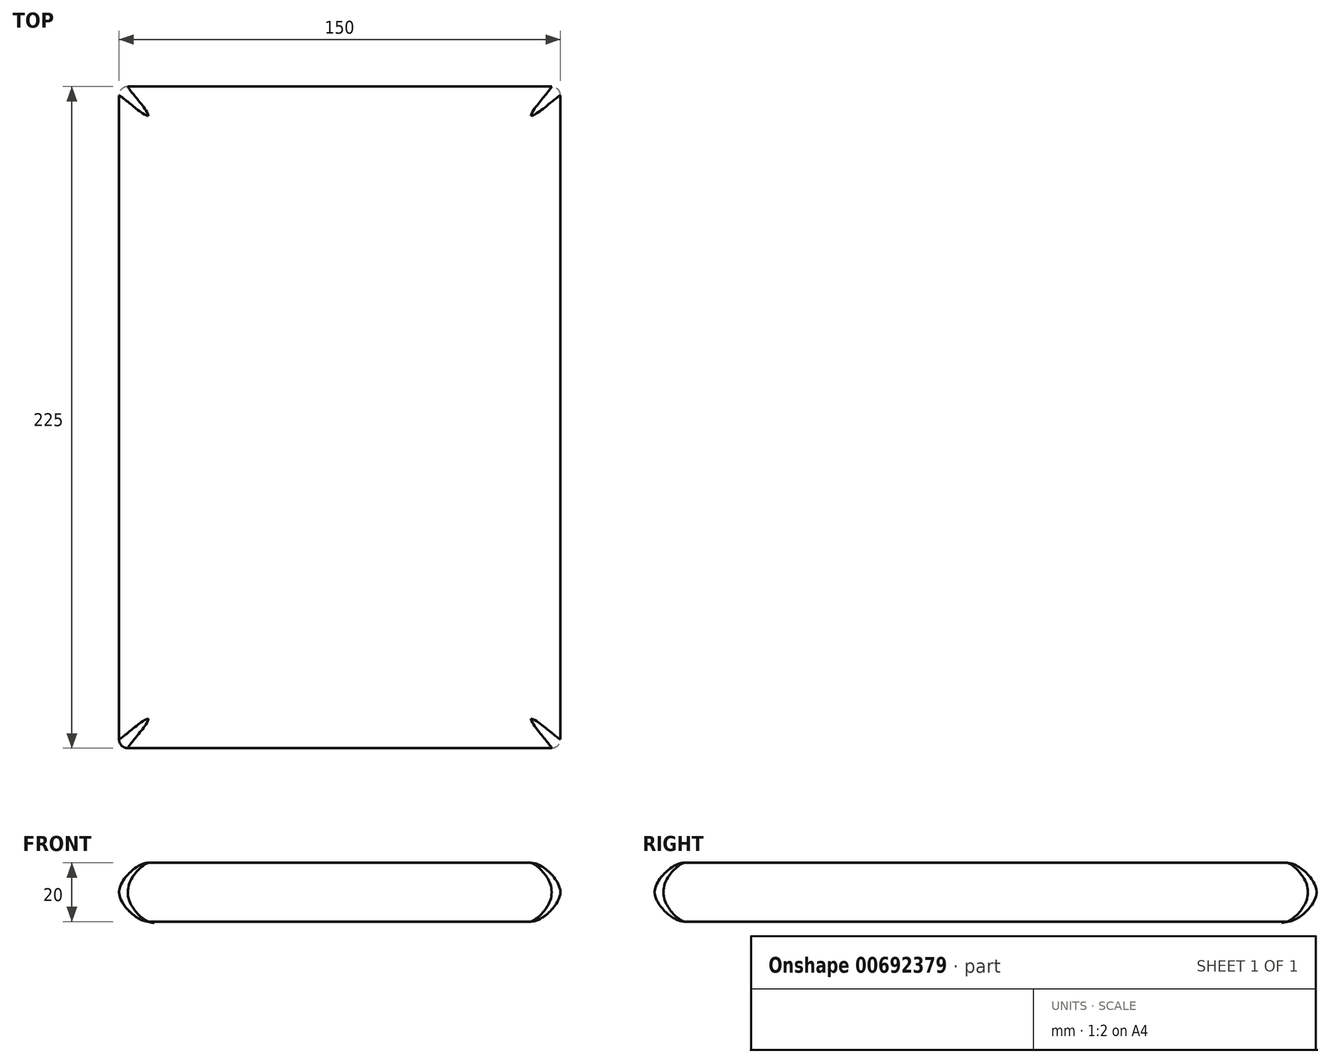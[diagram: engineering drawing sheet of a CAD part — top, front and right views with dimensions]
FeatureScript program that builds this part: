
annotation { "Feature Type Name" : "Feature", "Feature Type Description" : "" }
export const myFeature = defineFeature(function(context is Context, id is Id, definition is map)
    precondition{}
    {
        {
            var Q0;
            Q0=qCreatedBy(makeId("Right.planeOp"),FACE);
            var sketch = newSketch(context, id + "F0", { "sketchPlane" : qUnion([Q0])});
            skLineSegment(sketch, "E0.bottom", {"start": v(-112.5, 17.5) * mm, "end": v(-87.5, 17.5) * mm});
            skLineSegment(sketch, "E0.top", {"start": v(-112.5, 2.5) * mm, "end": v(-87.5, 2.5) * mm});
            skLineSegment(sketch, "E0.left", {"start": v(-112.5, 17.5) * mm, "end": v(-112.5, 2.5) * mm});
            skLineSegment(sketch, "E0.right", {"start": v(-87.5, 17.5) * mm, "end": v(-87.5, 2.5) * mm});
            skLineSegment(sketch, "E1.bottom", {"start": v(-132.5, 20) * mm, "end": v(0, 20) * mm});
            skLineSegment(sketch, "E1.top", {"start": v(-132.5, 0) * mm, "end": v(0, 0) * mm});
            skLineSegment(sketch, "E1.left", {"start": v(-132.5, 20) * mm, "end": v(-132.5, 0) * mm, "construction": true});
            skLineSegment(sketch, "E1.right", {"start": v(0, 20) * mm, "end": v(0, 0) * mm});
            skPoint(sketch, "E2", {"position": v(-112.5, 10) * mm});
            skPoint(sketch, "E3", {"position": v(-112.5, 20) * mm});
            skLineSegment(sketch, "E4", {"start": v(-112.5, 10) * mm, "end": v(-132.5, 10) * mm, "construction": true});
            skEllipticalArc(sketch, "E5", {});
            skLineSegment(sketch, "E6", {"start": v(-87.5, 17.5) * mm, "end": v(0, 17.5) * mm});
            skLineSegment(sketch, "E7", {"start": v(-87.5, 2.5) * mm, "end": v(0, 2.5) * mm});
            skLineSegment(sketch, "E8", {"start": v(0, 0) * mm, "end": v(0, -20.03) * mm, "construction": true});
            const initialGuessF0  = {"E5": [-0.1125, 0.01, -1, 0, 0.02, 0.01, 4.71238898038469, 1.5707963267948966]};
            skSetInitialGuess(sketch, initialGuessF0);
            skSolve(sketch);
        }
        {
            var Q0;
            Q0=qCreatedBy(makeId("Top.planeOp"),FACE);
            var sketch = newSketch(context, id + "F1", { "sketchPlane" : qUnion([Q0])});
            skLineSegment(sketch, "E9.bottom", {"start": v(-75, 112.5) * mm, "end": v(75, 112.5) * mm});
            skLineSegment(sketch, "E9.top", {"start": v(-75, -112.5) * mm, "end": v(75, -112.5) * mm});
            skLineSegment(sketch, "E9.left", {"start": v(-75, 112.5) * mm, "end": v(-75, -112.5) * mm});
            skLineSegment(sketch, "E9.right", {"start": v(75, 112.5) * mm, "end": v(75, -112.5) * mm});
            skPoint(sketch, "E10", {"position": v(0, 112.5) * mm});
            skPoint(sketch, "E11", {"position": v(-75, 0) * mm});
            skLineSegment(sketch, "E12", {"start": v(-75, 0) * mm, "end": v(0, 0) * mm, "construction": true});
            skLineSegment(sketch, "E13", {"start": v(0, 0) * mm, "end": v(0, 112.5) * mm, "construction": true});
            skSolve(sketch);
        }
        {
            var Q0;
            Q0=makeQuery(id+"F1.imprint","IMPRINT",FACE,{"disambiguationData":[TD([[makeQuery(id+"F1.imprint","IMPRINT",EDGE,{"derivedFrom":sQuery(id+"F1.wireOp",EDGE,"E9.bottom")}),-1.0]])]});
            extrude(context, id + "F2", {"entities" : qUnion([Q0]), "depth" : 20 * mm, "offsetDistance" : 25 * mm});
        }
        {
            var Q0;
            Q0=makeQuery(id+"F2.opExtrude","CAP_FACE",FACE,{"disambiguationData":[OSD([sQuery(id+"F1.wireOp",EDGE,"E9.bottom"),sQuery(id+"F1.wireOp",EDGE,"E9.top"),sQuery(id+"F1.wireOp",EDGE,"E9.left"),sQuery(id+"F1.wireOp",EDGE,"E9.right")])],"isStart":false});
            var Q1;
            Q1=makeQuery(id+"F2.opExtrude","CAP_FACE",FACE,{"disambiguationData":[OSD([sQuery(id+"F1.wireOp",EDGE,"E9.bottom"),sQuery(id+"F1.wireOp",EDGE,"E9.top"),sQuery(id+"F1.wireOp",EDGE,"E9.left"),sQuery(id+"F1.wireOp",EDGE,"E9.right")])],"isStart":true});
            fillet(context, id + "F3", {"entities" : qUnion([Q0, Q1]), "radius" : 10 * mm, "tangentPropagation" : true, "rho" : 0.3, "crossSection" : FilletCrossSection.CONIC, "allowEdgeOverflow" : false});
        }
        {
            var Q0;
            Q0=makeQuery(id+"F3.opFillet","BLEND_EDGE",EDGE,{"blendedFrom":[makeQuery(id+"F2.opExtrude","CAP_EDGE",EDGE,{"disambiguationData":[OSD([sQuery(id+"F1.wireOp",EDGE,"E9.top")])],"isStart":false}),makeQuery(id+"F2.opExtrude","CAP_EDGE",EDGE,{"disambiguationData":[OSD([sQuery(id+"F1.wireOp",EDGE,"E9.right")])],"isStart":false})],"blendedInto":[]});
            var Q1;
            Q1=makeQuery(id+"F3.opFillet","BLEND_EDGE",EDGE,{"blendedFrom":[makeQuery(id+"F2.opExtrude","CAP_EDGE",EDGE,{"disambiguationData":[OSD([sQuery(id+"F1.wireOp",EDGE,"E9.top")])],"isStart":false}),makeQuery(id+"F2.opExtrude","CAP_EDGE",EDGE,{"disambiguationData":[OSD([sQuery(id+"F1.wireOp",EDGE,"E9.left")])],"isStart":false})],"blendedInto":[]});
            var Q2;
            Q2=makeQuery(id+"F3.opFillet","BLEND_EDGE",EDGE,{"blendedFrom":[makeQuery(id+"F2.opExtrude","CAP_EDGE",EDGE,{"disambiguationData":[OSD([sQuery(id+"F1.wireOp",EDGE,"E9.bottom")])],"isStart":false}),makeQuery(id+"F2.opExtrude","CAP_EDGE",EDGE,{"disambiguationData":[OSD([sQuery(id+"F1.wireOp",EDGE,"E9.left")])],"isStart":false})],"blendedInto":[]});
            var Q3;
            Q3=makeQuery(id+"F3.opFillet","BLEND_EDGE",EDGE,{"blendedFrom":[makeQuery(id+"F2.opExtrude","CAP_EDGE",EDGE,{"disambiguationData":[OSD([sQuery(id+"F1.wireOp",EDGE,"E9.bottom")])],"isStart":false}),makeQuery(id+"F2.opExtrude","CAP_EDGE",EDGE,{"disambiguationData":[OSD([sQuery(id+"F1.wireOp",EDGE,"E9.right")])],"isStart":false})],"blendedInto":[]});
            fillet(context, id + "F4", {"entities" : qUnion([Q0, Q1, Q2, Q3]), "radius" : 3 * mm, "tangentPropagation" : true, "allowEdgeOverflow" : false});
        }
    });
